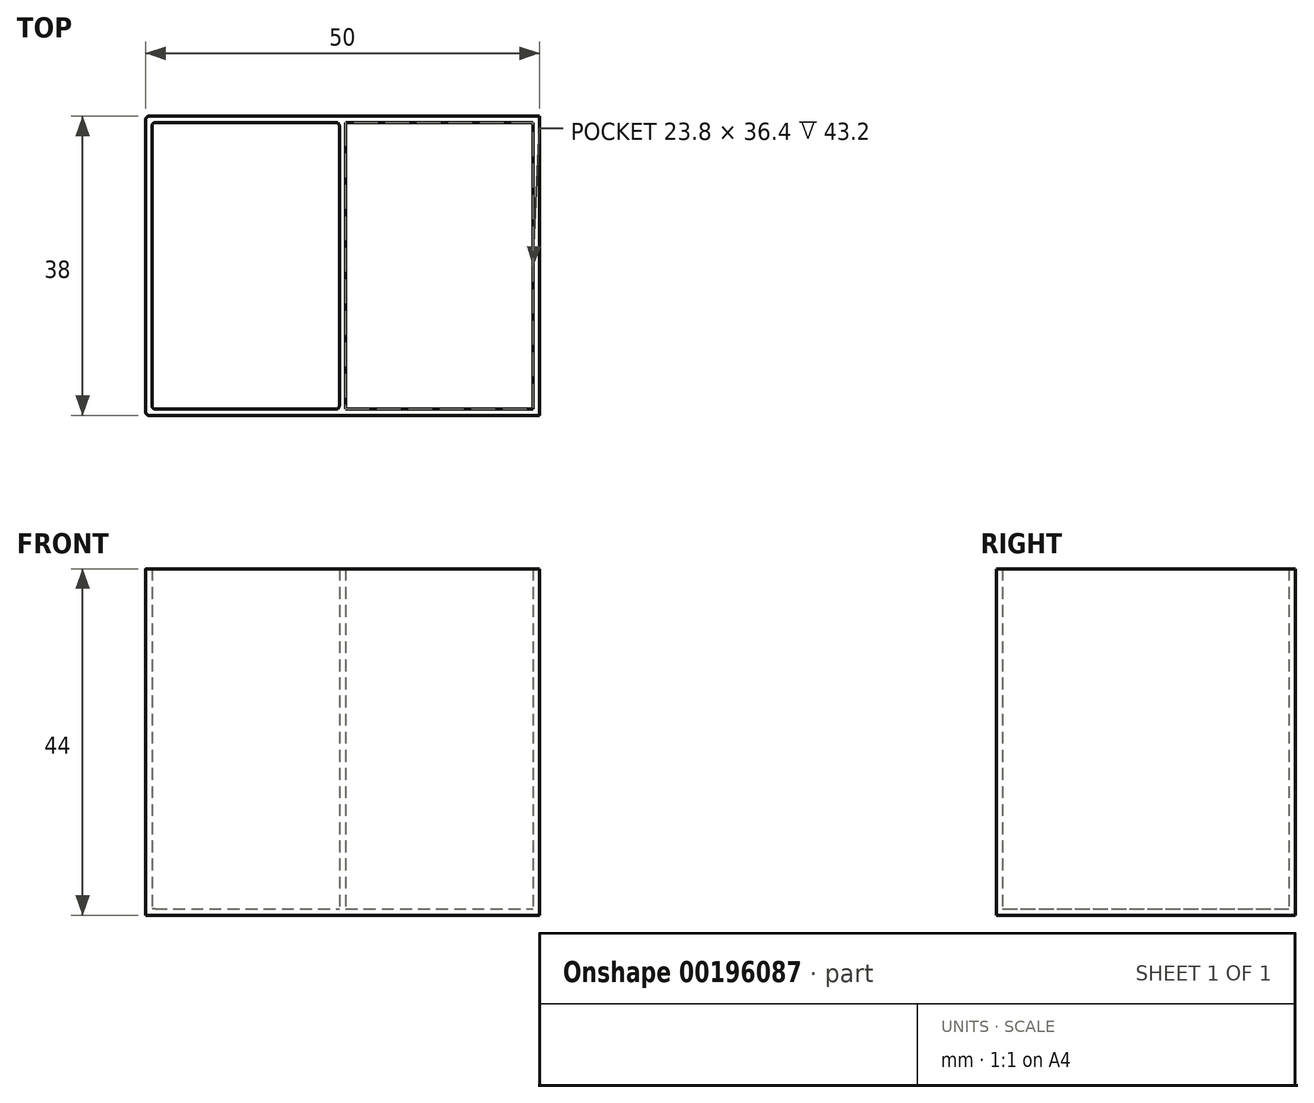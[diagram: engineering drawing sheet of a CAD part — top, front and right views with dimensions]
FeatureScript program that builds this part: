
annotation { "Feature Type Name" : "Feature", "Feature Type Description" : "" }
export const myFeature = defineFeature(function(context is Context, id is Id, definition is map)
    precondition{}
    {
        {
            var Q0;
            Q0=qCreatedBy(makeId("Top.planeOp"),FACE);
            var sketch = newSketch(context, id + "F0", { "sketchPlane" : qUnion([Q0])});
            skLineSegment(sketch, "E0.bottom", {"start": v(0, 0) * mm, "end": v(-50, 0) * mm});
            skLineSegment(sketch, "E0.top", {"start": v(0, 38) * mm, "end": v(-50, 38) * mm});
            skLineSegment(sketch, "E0.left", {"start": v(0, 0) * mm, "end": v(0, 38) * mm});
            skLineSegment(sketch, "E0.right", {"start": v(-50, 0) * mm, "end": v(-50, 38) * mm});
            skSolve(sketch);
        }
        {
            var Q0;
            Q0=makeQuery(id+"F0.imprint","IMPRINT",FACE,{"disambiguationData":[TD([[makeQuery(id+"F0.imprint","IMPRINT",EDGE,{"derivedFrom":sQuery(id+"F0.wireOp",EDGE,"E0.bottom")}),-1.0]])]});
            extrude(context, id + "F1", {"entities" : qUnion([Q0]), "depth" : 0.8 * mm});
        }
        {
            var Q0;
            Q0=makeQuery(id+"F1.opExtrude","CAP_FACE",FACE,{"disambiguationData":[OSD([sQuery(id+"F0.wireOp",EDGE,"E0.bottom"),sQuery(id+"F0.wireOp",EDGE,"E0.top"),sQuery(id+"F0.wireOp",EDGE,"E0.left"),sQuery(id+"F0.wireOp",EDGE,"E0.right")])],"isStart":false});
            var sketch = newSketch(context, id + "F2", { "sketchPlane" : qUnion([Q0])});
            skLineSegment(sketch, "E1", {"start": v(-50, 0) * mm, "end": v(0, 0) * mm});
            skLineSegment(sketch, "E2", {"start": v(0, 0) * mm, "end": v(0, 38) * mm});
            skLineSegment(sketch, "E3", {"start": v(0, 38) * mm, "end": v(-50, 38) * mm});
            skLineSegment(sketch, "E4", {"start": v(-50, 38) * mm, "end": v(-50, 0) * mm});
            skLineSegment(sketch, "E5.bottom", {"start": v(-49.2, 0.8) * mm, "end": v(-25.4, 0.8) * mm});
            skLineSegment(sketch, "E5.top", {"start": v(-49.2, 37.2) * mm, "end": v(-25.4, 37.2) * mm});
            skLineSegment(sketch, "E5.left", {"start": v(-49.2, 0.8) * mm, "end": v(-49.2, 37.2) * mm});
            skLineSegment(sketch, "E5.right", {"start": v(-0.8, 0.8) * mm, "end": v(-0.8, 37.2) * mm});
            skLineSegment(sketch, "E6", {"start": v(-25, 0.8) * mm, "end": v(-25, 37.2) * mm, "construction": true});
            skLineSegment(sketch, "E7", {"start": v(-25.4, 0.8) * mm, "end": v(-25.4, 37.2) * mm});
            skLineSegment(sketch, "E8", {"start": v(-24.6, 0.8) * mm, "end": v(-24.6, 37.2) * mm});
            skLineSegment(sketch, "E9.trimOffspring", {"start": v(-24.6, 0.8) * mm, "end": v(-0.8, 0.8) * mm});
            skLineSegment(sketch, "E10.trimOffspring", {"start": v(-24.6, 37.2) * mm, "end": v(-0.8, 37.2) * mm});
            skSolve(sketch);
        }
        {
            var Q0;
            Q0=makeQuery(id+"F2.imprint","IMPRINT",FACE,{"disambiguationData":[TD([[makeQuery(id+"F2.imprint","IMPRINT",EDGE,{"derivedFrom":sQuery(id+"F2.wireOp",EDGE,"E1")}),-1.0]])]});
            extrude(context, id + "F3", {"entities" : qUnion([Q0]), "operationType" : NewBodyOperationType.ADD, "depth" : (44 - 0.8) * mm});
        }
        {
            var Q0;
            Q0=makeQuery(id+"F3.boolean.opBoolean","MERGE",EDGE,{"derivedFrom":[makeQuery(id+"F1.opExtrude","SWEPT_EDGE",EDGE,{"disambiguationData":[OSD([sQuery(id+"F0.wireOp",EDGE,"E0.bottom"),sQuery(id+"F0.wireOp",EDGE,"E0.right")])]}),makeQuery(id+"F3.opExtrude","SWEPT_EDGE",EDGE,{"disambiguationData":[OSD([sQuery(id+"F2.wireOp",EDGE,"E1"),sQuery(id+"F2.wireOp",EDGE,"E4")])]})]});
            var Q1;
            Q1=makeQuery(id+"F3.opExtrude","SWEPT_EDGE",EDGE,{"disambiguationData":[OSD([sQuery(id+"F2.wireOp",EDGE,"E5.bottom"),sQuery(id+"F2.wireOp",EDGE,"E5.left")])]});
            var Q2;
            Q2=makeQuery(id+"F3.opExtrude","SWEPT_EDGE",EDGE,{"disambiguationData":[OSD([sQuery(id+"F2.wireOp",EDGE,"E5.top"),sQuery(id+"F2.wireOp",EDGE,"E5.left")])]});
            var Q3;
            Q3=makeQuery(id+"F3.boolean.opBoolean","MERGE",EDGE,{"derivedFrom":[makeQuery(id+"F1.opExtrude","SWEPT_EDGE",EDGE,{"disambiguationData":[OSD([sQuery(id+"F0.wireOp",EDGE,"E0.top"),sQuery(id+"F0.wireOp",EDGE,"E0.right")])]}),makeQuery(id+"F3.opExtrude","SWEPT_EDGE",EDGE,{"disambiguationData":[OSD([sQuery(id+"F2.wireOp",EDGE,"E3"),sQuery(id+"F2.wireOp",EDGE,"E4")])]})]});
            var Q4;
            Q4=makeQuery(id+"F3.opExtrude","SWEPT_EDGE",EDGE,{"disambiguationData":[OSD([sQuery(id+"F2.wireOp",EDGE,"E5.top"),sQuery(id+"F2.wireOp",EDGE,"E7")])]});
            var Q5;
            Q5=makeQuery(id+"F3.opExtrude","SWEPT_EDGE",EDGE,{"disambiguationData":[OSD([sQuery(id+"F2.wireOp",EDGE,"E5.bottom"),sQuery(id+"F2.wireOp",EDGE,"E7")])]});
            fillet(context, id + "F4", {"entities" : qUnion([Q0, Q1, Q2, Q3, Q4, Q5]), "radius" : 0.4 * mm, "tangentPropagation" : true, "allowEdgeOverflow" : false});
        }
    });
